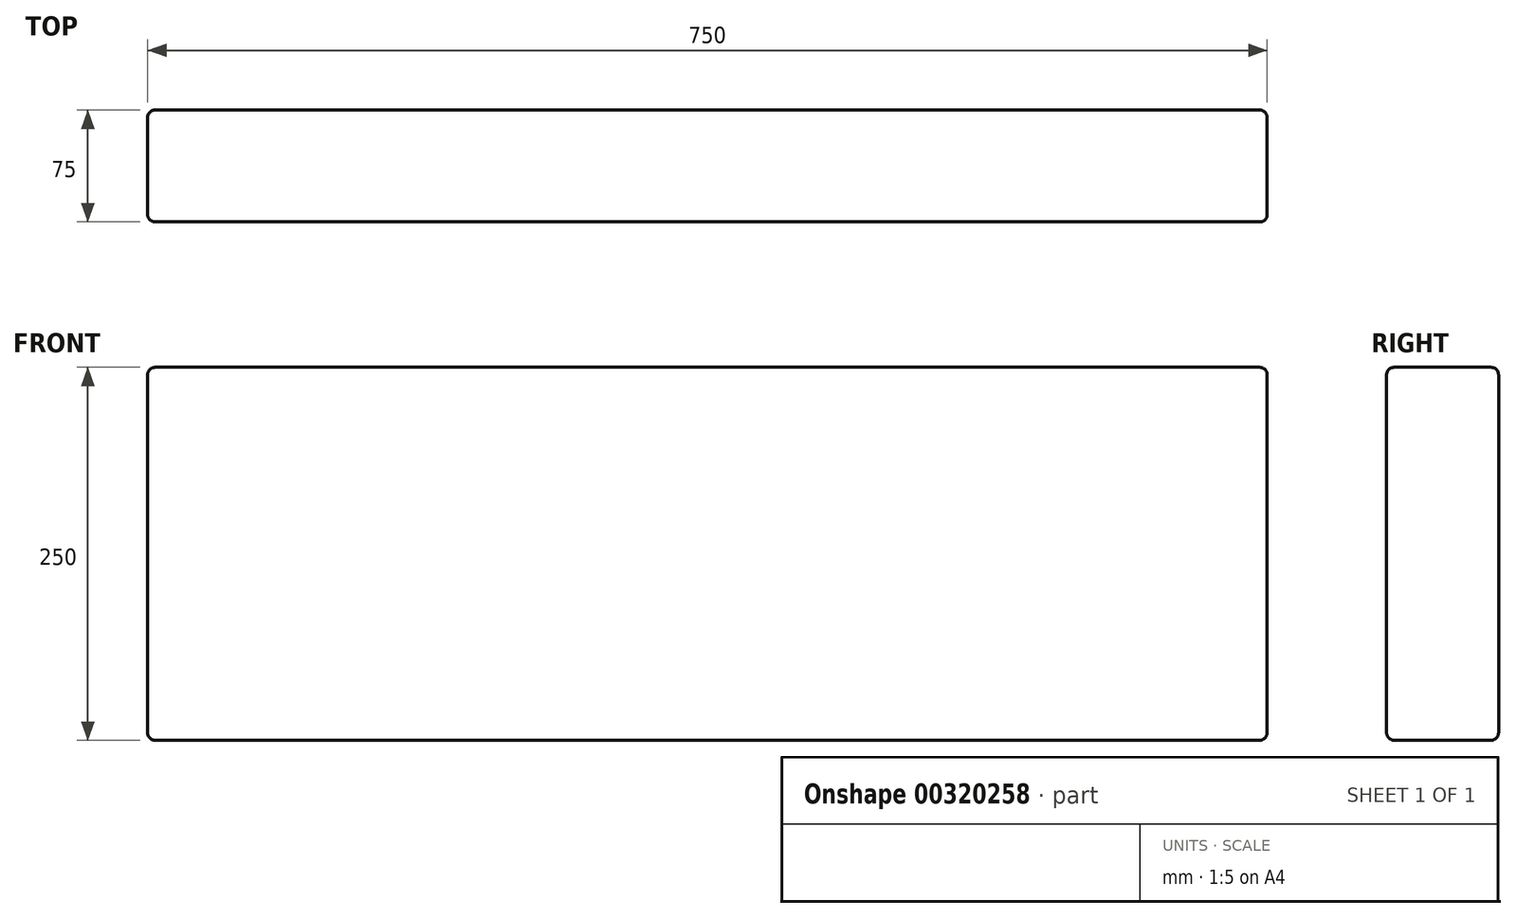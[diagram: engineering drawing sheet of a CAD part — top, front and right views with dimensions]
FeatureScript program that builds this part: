
annotation { "Feature Type Name" : "Feature", "Feature Type Description" : "" }
export const myFeature = defineFeature(function(context is Context, id is Id, definition is map)
    precondition{}
    {
        {
            var Q0;
            Q0=qCreatedBy(makeId("Front.planeOp"),FACE);
            var sketch = newSketch(context, id + "F0", { "sketchPlane" : qUnion([Q0])});
            skLineSegment(sketch, "E0.bottom", {"start": v(375, -125) * mm, "end": v(-375, -125) * mm});
            skLineSegment(sketch, "E0.top", {"start": v(375, 125) * mm, "end": v(-375, 125) * mm});
            skLineSegment(sketch, "E0.left", {"start": v(375, -125) * mm, "end": v(375, 125) * mm});
            skLineSegment(sketch, "E0.right", {"start": v(-375, -125) * mm, "end": v(-375, 125) * mm});
            skPoint(sketch, "E0.middle", {"position": v(0, 0) * mm});
            skSolve(sketch);
        }
        {
            var Q0;
            Q0 = qSketchRegion(id + "F0", true);
            extrude(context, id + "F1", {"entities" : qUnion([Q0]), "endBound" : BoundingType.SYMMETRIC, "depth" : 75 * mm});
        }
        {
            var Q0;
            Q0=makeQuery(id+"F1.opExtrude","SWEPT_FACE",FACE,{"disambiguationData":[OSD([sQuery(id+"F0.wireOp",EDGE,"E0.right")])]});
            var Q1;
            Q1=makeQuery(id+"F1.opExtrude","CAP_FACE",FACE,{"disambiguationData":[OSD([sQuery(id+"F0.wireOp",EDGE,"E0.bottom"),sQuery(id+"F0.wireOp",EDGE,"E0.top"),sQuery(id+"F0.wireOp",EDGE,"E0.left"),sQuery(id+"F0.wireOp",EDGE,"E0.right")])],"isStart":true});
            var Q2;
            Q2=makeQuery(id+"F1.opExtrude","SWEPT_FACE",FACE,{"disambiguationData":[OSD([sQuery(id+"F0.wireOp",EDGE,"E0.top")])]});
            var Q3;
            Q3=makeQuery(id+"F1.opExtrude","CAP_FACE",FACE,{"disambiguationData":[OSD([sQuery(id+"F0.wireOp",EDGE,"E0.bottom"),sQuery(id+"F0.wireOp",EDGE,"E0.top"),sQuery(id+"F0.wireOp",EDGE,"E0.left"),sQuery(id+"F0.wireOp",EDGE,"E0.right")])],"isStart":false});
            var Q4;
            Q4=makeQuery(id+"F1.opExtrude","CAP_EDGE",EDGE,{"disambiguationData":[OSD([sQuery(id+"F0.wireOp",EDGE,"E0.bottom")])],"isStart":true});
            var Q5;
            Q5=makeQuery(id+"F1.opExtrude","SWEPT_FACE",FACE,{"disambiguationData":[OSD([sQuery(id+"F0.wireOp",EDGE,"E0.left")])]});
            fillet(context, id + "F2", {"entities" : qUnion([Q0, Q1, Q2, Q3, Q4, Q5]), "radius" : 5 * mm, "tangentPropagation" : true, "allowEdgeOverflow" : false});
        }
    });
